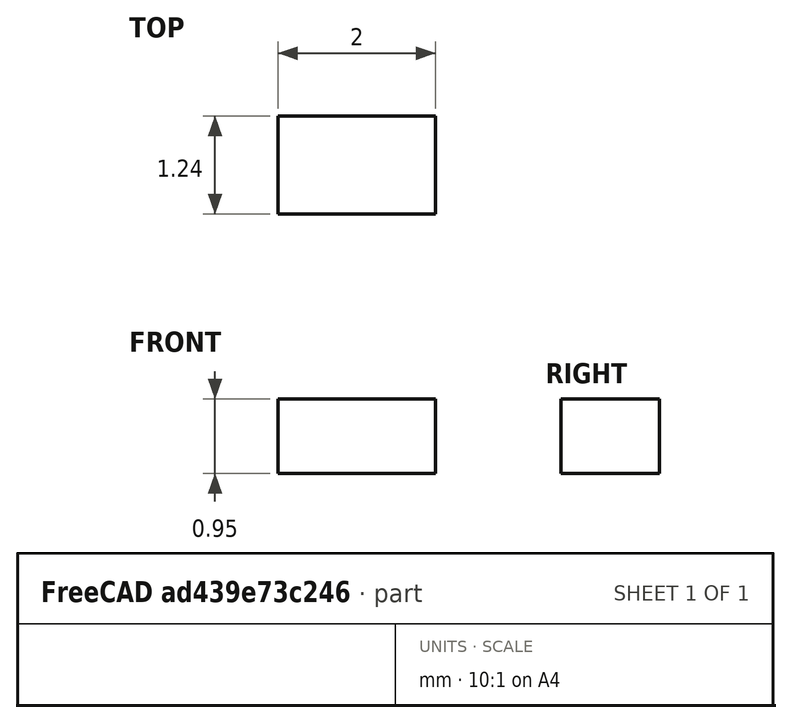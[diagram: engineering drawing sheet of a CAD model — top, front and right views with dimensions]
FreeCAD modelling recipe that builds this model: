
FCSTD DOCUMENT  (FreeCAD 0.16R6707 (Git))
Label: LF2012
License: All rights reserved
LicenseURL: http://en.wikipedia.org/wiki/All_rights_reserved
objects: Sketcher::SketchObject×1, PartDesign::Pad×1
note: 3 computed .brp shape members not serialized (recipe doc carries the construction recipe); baked Part::Feature solids carry a one-line shape summary decoded from their .brp

FEATURE [Sketcher::SketchObject] Sketch
  sketch-geometry (5):
    g0: LineSegment StartX=-1 StartY=0.625 StartZ=0 EndX=1 EndY=0.625 EndZ=0
    g1: LineSegment StartX=1 StartY=0.625 StartZ=0 EndX=1 EndY=-0.625 EndZ=0
    g2: LineSegment StartX=1 StartY=-0.625 StartZ=0 EndX=-1 EndY=-0.625 EndZ=0
    g3: LineSegment StartX=-1 StartY=-0.625 StartZ=0 EndX=-1 EndY=0.625 EndZ=0
    g4: LineSegment [constr] StartX=0 StartY=0 StartZ=0 EndX=0 EndY=2.06425 EndZ=0
  constraints (14):
    c: Coincident(g0,g1)
    c: Coincident(g1,g2)
    c: Coincident(g2,g3)
    c: Coincident(g3,g0)
    c: Horizontal(g0)
    c: Horizontal(g2)
    c: Vertical(g1)
    c: Vertical(g3)
    c: DistanceX(g0,g0) = 2
    c: DistanceY(g3,g3) = 1.25
    c: Coincident(g4,g-1)
    c: Vertical(g4)
    c: Symmetric(g0,g0,g4)
    c: Symmetric(g1,g0,g-1)
FEATURE [PartDesign::Pad] Pad
  Length = 0.95
  Length2 = 100
  Sketch = -> Sketch
  Type = 0
